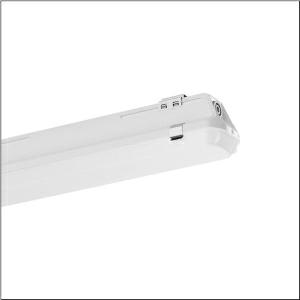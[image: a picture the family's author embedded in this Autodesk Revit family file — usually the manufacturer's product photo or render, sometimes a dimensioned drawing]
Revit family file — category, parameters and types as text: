
# Revit family: monsun_r__21_51fb10dp360b_a0ac
name_source: partatom
category: Lighting Fixtures
units: mm (PartAtom-declared; Revit-internal decimal feet)

## family parameters
Cut with Voids When Loaded = No
Host = Face
Light Source = No
Part Type = Normal
Room Calculation Point = No
Round Connector Dimension = Use Diameter
Shared = No

## types (1)
- --- (1 x LED, 6060 lm, 43.2 W, 3000K)
    Apparent Load = 43 VA
    CIE Flux Codes = 47 77 93 94 100
    Color Rendering = 80
    Color Temperature = 3000K
    Default Elevation = 1800 mm
    Description = Monsun® 21, damp-proof luminaire, chain hanger, primary optical cover: enclosure, of PMMA, light emission: direct distribution, primary light characteristic: symmetric, installation type: suspended mounting, surface-mounted, horizontal mounting, vertical mounting, LED, rated luminous flux: 6.060lm, luminous efficacy: 154lm/W, light colour: 830, colour temperature: 3000K, control gear: ECG DALI, with terminal, 5-pole, max. 2.5mm², mains connection: 220..240V, AC, 50/60Hz, rated input power: 39W, housing, of glass-fibre reinforced polyester, uncoated, bright grey, incl. chain hanger, length: 1.590mm, width: 90mm, height: 88mm, clip for enclosure, of stainless steel (V2A), ceiling mounting element, of stainless steel (V2A), chain hanger, of stainless steel (V2A), protection rating (complete): IP66, insulation class (complete): insulation class I (protective earthing), certification: CE, ENEC, VDE, UKCA, protection symbol: D, impact resistance: IK04, permissible operating ambient temperature: -25..+35°C, standard: EN 50419, EN 60598-2-1, corresponds to IFS (International Featured Standards) requirements for safety and quality in the food industry, for indoor or canopied outdoor use, no direct snow, no direct sun, no direct rain, contact your sales advisor before using the luminaires in applications with unclear chemical exposure, large temperature fluctuations or condensation-forming humidity, LABS conformity tested according to VDMA 24364:2018-05, packaging unit: 1 piece
    Height = 89 mm
    Lamp = 1 x LED
    Lamp Light Flux = 6060 lm
    Lamp Power = 43.2 W
    Lamp count = 1
    Length = 1590 mm
    Luminous efficacy = 140 lm/W
    Manufacturer = Siteco
    ModVariant = No
    Model = 51FB10DP360B
    Mounting Place = Ceiling
    Mounting Type = Surface mounted
    Number of Poles = 1
    OnlyDefault = Yes
    Power Factor = 1
    Product Name = Monsun® 21
    Product group = damp-proof luminaire
    ProductGroupID = 301
    Protection Class = Protection class I
    Protection Degree = IP 66
    RLX_Detail_Level = 1
    RLX_Emergency_Light_Flux = 0 lm
    RLX_Emergency_Type = 0
    RLX_Emergency_Type_DB = No
    RlxData = <blob elided: 92329 chars, md5=b711155f>
    Socket = socket
    Standby Power = 0 W
    System Light Flux = 6060 lm
    System Power = 43 W
    Type Comments = factory setting: luminous flux: 100 % | dim-lin: 254 | 286 mA
    Type Image = l_1006717.jpg
    URL = http://relux.com
    VarID = @adj_096537
    Voltage = 0 V
    Weight = 0.00 kg
    Width = 90 mm

## geometry (parser evidence)
native form markers: Blend x4, Sweep x12
no freeform markers — native parametric forms only
